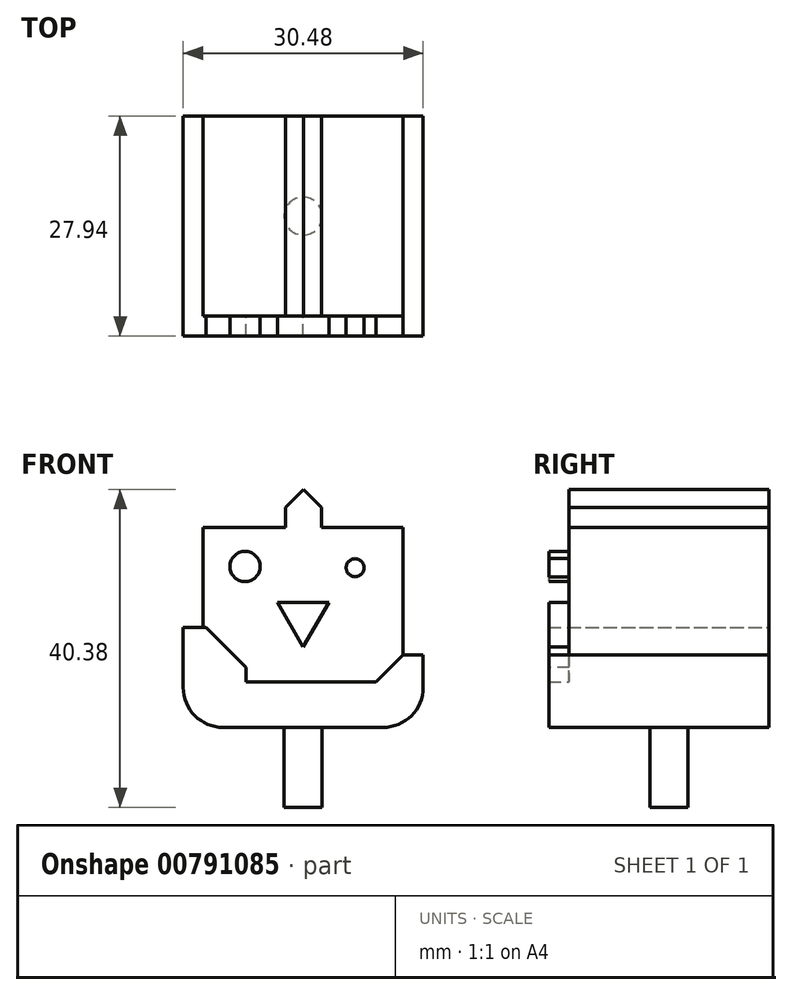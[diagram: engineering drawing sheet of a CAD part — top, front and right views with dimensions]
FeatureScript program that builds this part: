
annotation { "Feature Type Name" : "Feature", "Feature Type Description" : "" }
export const myFeature = defineFeature(function(context is Context, id is Id, definition is map)
    precondition{}
    {
        {
            var Q0;
            Q0=qCreatedBy(makeId("Top.planeOp"),FACE);
            var sketch = newSketch(context, id + "F0", { "sketchPlane" : qUnion([Q0])});
            skLineSegment(sketch, "E0.bottom", {"start": v(-12.7, 12.7) * mm, "end": v(12.7, 12.7) * mm});
            skLineSegment(sketch, "E0.top", {"start": v(-12.7, -12.7) * mm, "end": v(12.7, -12.7) * mm});
            skLineSegment(sketch, "E0.left", {"start": v(-12.7, 12.7) * mm, "end": v(-12.7, -12.7) * mm});
            skLineSegment(sketch, "E0.right", {"start": v(12.7, 12.7) * mm, "end": v(12.7, -12.7) * mm});
            skPoint(sketch, "E0.middle", {"position": v(0, 0) * mm});
            skSolve(sketch);
        }
        {
            var Q0;
            Q0 = qSketchRegion(id + "F0", true);
            extrude(context, id + "F1", {"entities" : qUnion([Q0]), "oppositeDirection" : true, "depth" : 25.4 * mm, "offsetDistance" : 25.4 * mm});
        }
        {
            var Q0;
            Q0=makeQuery(id+"F1.opExtrude","SWEPT_FACE",FACE,{"disambiguationData":[OSD([sQuery(id+"F0.wireOp",EDGE,"E0.top")])]});
            var sketch = newSketch(context, id + "F2", { "sketchPlane" : qUnion([Q0])});
            skLineSegment(sketch, "E1.bottom", {"start": v(-12.7, -25.4) * mm, "end": v(12.7, -25.4) * mm});
            skLineSegment(sketch, "E1.top", {"start": v(-12.7, -19.64) * mm, "end": v(12.7, -19.64) * mm});
            skLineSegment(sketch, "E1.left", {"start": v(-12.7, -25.4) * mm, "end": v(-12.7, -19.64) * mm});
            skLineSegment(sketch, "E1.right", {"start": v(12.7, -25.4) * mm, "end": v(12.7, -19.64) * mm});
            skLineSegment(sketch, "E2.bottom", {"start": v(7.61, -19.64) * mm, "end": v(12.7, -19.64) * mm});
            skLineSegment(sketch, "E2.top", {"start": v(7.61, -16.18) * mm, "end": v(12.7, -16.18) * mm});
            skLineSegment(sketch, "E2.left", {"start": v(7.61, -19.64) * mm, "end": v(7.61, -16.18) * mm});
            skLineSegment(sketch, "E2.right", {"start": v(12.7, -19.64) * mm, "end": v(12.7, -16.18) * mm});
            skLineSegment(sketch, "E3.bottom", {"start": v(-7.28, -19.64) * mm, "end": v(-12.7, -19.64) * mm});
            skLineSegment(sketch, "E3.top", {"start": v(-7.28, -12.7) * mm, "end": v(-12.7, -12.7) * mm});
            skLineSegment(sketch, "E3.left", {"start": v(-7.28, -19.64) * mm, "end": v(-7.28, -12.7) * mm});
            skLineSegment(sketch, "E3.right", {"start": v(-12.7, -19.64) * mm, "end": v(-12.7, -12.7) * mm});
            skSolve(sketch);
        }
        {
            var Q0;
            Q0 = qSketchRegion(id + "F2", true);
            extrude(context, id + "F3", {"entities" : qUnion([Q0]), "operationType" : NewBodyOperationType.ADD, "depth" : 2.54 * mm, "offsetDistance" : 25.4 * mm});
        }
        {
            var Q0;
            Q0=makeQuery(id+"F1.opExtrude","SWEPT_FACE",FACE,{"disambiguationData":[OSD([sQuery(id+"F0.wireOp",EDGE,"E0.top")])]});
            var sketch = newSketch(context, id + "F4", { "sketchPlane" : qUnion([Q0])});
            skCircle(sketch, "E4", {"center": v(-7.38, -4.96) * mm, "radius": 1.93 * mm});
            skCircle(sketch, "E5", {"center": v(6.6, -5.1) * mm, "radius": 1.15 * mm});
            skSolve(sketch);
        }
        {
            var Q0;
            Q0 = qSketchRegion(id + "F4", true);
            extrude(context, id + "F5", {"entities" : qUnion([Q0]), "operationType" : NewBodyOperationType.ADD, "depth" : 2.54 * mm, "offsetDistance" : 25.4 * mm});
        }
        {
            var Q0;
            Q0=makeQuery(id+"F1.opExtrude","SWEPT_FACE",FACE,{"disambiguationData":[OSD([sQuery(id+"F0.wireOp",EDGE,"E0.top")])]});
            var sketch = newSketch(context, id + "F6", { "sketchPlane" : qUnion([Q0])});
            skCircle(sketch, "E6.cCircle", {"center": v(0, -11.4) * mm, "radius": 1.9 * mm, "construction": true});
            skLineSegment(sketch, "E6.0", {"start": v(-3.29, -9.5) * mm, "end": v(3.29, -9.5) * mm});
            skLineSegment(sketch, "E6.1", {"start": v(3.29, -9.5) * mm, "end": v(0, -15.19) * mm});
            skLineSegment(sketch, "E6.2", {"start": v(0, -15.19) * mm, "end": v(-3.29, -9.5) * mm});
            skPoint(sketch, "E6.0.midPoint", {"position": v(0, -9.5) * mm});
            skSolve(sketch);
        }
        {
            var Q0;
            Q0 = qSketchRegion(id + "F6", true);
            extrude(context, id + "F7", {"entities" : qUnion([Q0]), "operationType" : NewBodyOperationType.ADD, "depth" : 2.54 * mm, "offsetDistance" : 25.4 * mm});
        }
        {
            var Q0;
            Q0=makeQuery(id+"F3.boolean.opBoolean","MERGE",FACE,{"derivedFrom":[makeQuery(id+"F1.opExtrude","SWEPT_FACE",FACE,{"disambiguationData":[OSD([sQuery(id+"F0.wireOp",EDGE,"E0.right")])]}),makeQuery(id+"F3.opExtrude","SWEPT_FACE",FACE,{"disambiguationData":[OSD([sQuery(id+"F2.wireOp",EDGE,"E1.right"),sQuery(id+"F2.wireOp",EDGE,"E2.right")])]})]});
            var sketch = newSketch(context, id + "F8", { "sketchPlane" : qUnion([Q0])});
            skLineSegment(sketch, "E7.bottom", {"start": v(-15.24, -16.18) * mm, "end": v(12.7, -16.18) * mm});
            skLineSegment(sketch, "E7.top", {"start": v(-15.24, -25.4) * mm, "end": v(12.7, -25.4) * mm});
            skLineSegment(sketch, "E7.left", {"start": v(-15.24, -16.18) * mm, "end": v(-15.24, -25.4) * mm});
            skLineSegment(sketch, "E7.right", {"start": v(12.7, -16.18) * mm, "end": v(12.7, -25.4) * mm});
            skSolve(sketch);
        }
        {
            var Q0;
            Q0 = qSketchRegion(id + "F8", true);
            extrude(context, id + "F9", {"entities" : qUnion([Q0]), "operationType" : NewBodyOperationType.ADD, "depth" : 2.54 * mm, "offsetDistance" : 25.4 * mm});
        }
        {
            var Q0;
            Q0=makeQuery(id+"F3.boolean.opBoolean","MERGE",FACE,{"derivedFrom":[makeQuery(id+"F1.opExtrude","SWEPT_FACE",FACE,{"disambiguationData":[OSD([sQuery(id+"F0.wireOp",EDGE,"E0.left")])]}),makeQuery(id+"F3.opExtrude","SWEPT_FACE",FACE,{"disambiguationData":[OSD([sQuery(id+"F2.wireOp",EDGE,"E1.left"),sQuery(id+"F2.wireOp",EDGE,"E3.right")])]})]});
            var sketch = newSketch(context, id + "F10", { "sketchPlane" : qUnion([Q0])});
            skLineSegment(sketch, "E8.bottom", {"start": v(15.24, -25.4) * mm, "end": v(-12.7, -25.4) * mm});
            skLineSegment(sketch, "E8.top", {"start": v(15.24, -12.7) * mm, "end": v(-12.7, -12.7) * mm});
            skLineSegment(sketch, "E8.left", {"start": v(15.24, -25.4) * mm, "end": v(15.24, -12.7) * mm});
            skLineSegment(sketch, "E8.right", {"start": v(-12.7, -25.4) * mm, "end": v(-12.7, -12.7) * mm});
            skSolve(sketch);
        }
        {
            var Q0;
            Q0 = qSketchRegion(id + "F10", true);
            extrude(context, id + "F11", {"entities" : qUnion([Q0]), "operationType" : NewBodyOperationType.ADD, "depth" : 2.54 * mm, "offsetDistance" : 25.4 * mm});
        }
        {
            var Q0;
            Q0=makeQuery(id+"F3.opExtrude","SWEPT_EDGE",EDGE,{"disambiguationData":[OSD([sQuery(id+"F2.wireOp",EDGE,"E3.top"),sQuery(id+"F2.wireOp",EDGE,"E3.left")])]});
            var Q1;
            Q1=makeQuery(id+"F3.opExtrude","SWEPT_EDGE",EDGE,{"disambiguationData":[OSD([sQuery(id+"F2.wireOp",EDGE,"E2.top"),sQuery(id+"F2.wireOp",EDGE,"E2.left")])]});
            chamfer(context, id + "F12", {"entities" : qUnion([Q0, Q1]), "width" : 5.08 * mm, "tangentPropagation" : true});
        }
        {
            var Q0;
            Q0=makeQuery(id+"F1.opExtrude","CAP_FACE",FACE,{"disambiguationData":[OSD([sQuery(id+"F0.wireOp",EDGE,"E0.bottom"),sQuery(id+"F0.wireOp",EDGE,"E0.top"),sQuery(id+"F0.wireOp",EDGE,"E0.left"),sQuery(id+"F0.wireOp",EDGE,"E0.right")])],"isStart":true});
            var sketch = newSketch(context, id + "F13", { "sketchPlane" : qUnion([Q0])});
            skLineSegment(sketch, "E9.bottom", {"start": v(-2.24, 12.7) * mm, "end": v(2.32, 12.7) * mm});
            skLineSegment(sketch, "E9.top", {"start": v(-2.24, -12.7) * mm, "end": v(2.32, -12.7) * mm});
            skLineSegment(sketch, "E9.left", {"start": v(-2.24, 12.7) * mm, "end": v(-2.24, -12.7) * mm});
            skLineSegment(sketch, "E9.right", {"start": v(2.32, 12.7) * mm, "end": v(2.32, -12.7) * mm});
            skSolve(sketch);
        }
        {
            var Q0;
            Q0 = qSketchRegion(id + "F13", true);
            extrude(context, id + "F14", {"entities" : qUnion([Q0]), "operationType" : NewBodyOperationType.ADD, "depth" : 5.08 * mm, "offsetDistance" : 25.4 * mm});
        }
        {
            var Q0;
            Q0=makeQuery(id+"F14.opExtrude","CAP_EDGE",EDGE,{"disambiguationData":[OSD([sQuery(id+"F13.wireOp",EDGE,"E9.right")])],"isStart":false});
            var Q1;
            Q1=makeQuery(id+"F14.opExtrude","CAP_EDGE",EDGE,{"disambiguationData":[OSD([sQuery(id+"F13.wireOp",EDGE,"E9.left")])],"isStart":false});
            chamfer(context, id + "F15", {"entities" : qUnion([Q0, Q1]), "width" : 2.54 * mm, "tangentPropagation" : true});
        }
        {
            var Q0;
            Q0=makeQuery(id+"F9.opExtrude","CAP_EDGE",EDGE,{"disambiguationData":[OSD([sQuery(id+"F8.wireOp",EDGE,"E7.top")])],"isStart":false});
            var Q1;
            Q1=makeQuery(id+"F11.opExtrude","CAP_EDGE",EDGE,{"disambiguationData":[OSD([sQuery(id+"F10.wireOp",EDGE,"E8.bottom")])],"isStart":false});
            fillet(context, id + "F16", {"entities" : qUnion([Q0, Q1]), "radius" : 5.08 * mm, "tangentPropagation" : true, "allowEdgeOverflow" : false});
        }
        {
            var Q0;
            Q0=makeQuery(id+"F11.boolean.opBoolean","MERGE",FACE,{"derivedFrom":[makeQuery(id+"F9.boolean.opBoolean","MERGE",FACE,{"derivedFrom":[makeQuery(id+"F3.boolean.opBoolean","MERGE",FACE,{"derivedFrom":[makeQuery(id+"F1.opExtrude","CAP_FACE",FACE,{"disambiguationData":[OSD([sQuery(id+"F0.wireOp",EDGE,"E0.bottom"),sQuery(id+"F0.wireOp",EDGE,"E0.top"),sQuery(id+"F0.wireOp",EDGE,"E0.left"),sQuery(id+"F0.wireOp",EDGE,"E0.right")])],"isStart":false}),makeQuery(id+"F3.opExtrude","SWEPT_FACE",FACE,{"disambiguationData":[OSD([sQuery(id+"F2.wireOp",EDGE,"E1.bottom")])]})]}),makeQuery(id+"F9.opExtrude","SWEPT_FACE",FACE,{"disambiguationData":[OSD([sQuery(id+"F8.wireOp",EDGE,"E7.top")])]})]}),makeQuery(id+"F11.opExtrude","SWEPT_FACE",FACE,{"disambiguationData":[OSD([sQuery(id+"F10.wireOp",EDGE,"E8.bottom")])]})]});
            var sketch = newSketch(context, id + "F17", { "sketchPlane" : qUnion([Q0])});
            skCircle(sketch, "E10", {"center": v(0, 0) * mm, "radius": 2.41 * mm});
            skSolve(sketch);
        }
        {
            var Q0;
            Q0=makeQuery(id+"F17.imprint","IMPRINT",FACE,{"disambiguationData":[TD([[makeQuery(id+"F17.imprint","IMPRINT",EDGE,{"derivedFrom":sQuery(id+"F17.wireOp",EDGE,"E10")}),1.0]])]});
            extrude(context, id + "F18", {"entities" : qUnion([Q0]), "operationType" : NewBodyOperationType.ADD, "depth" : 10.16 * mm, "offsetDistance" : 25.4 * mm});
        }
    });
